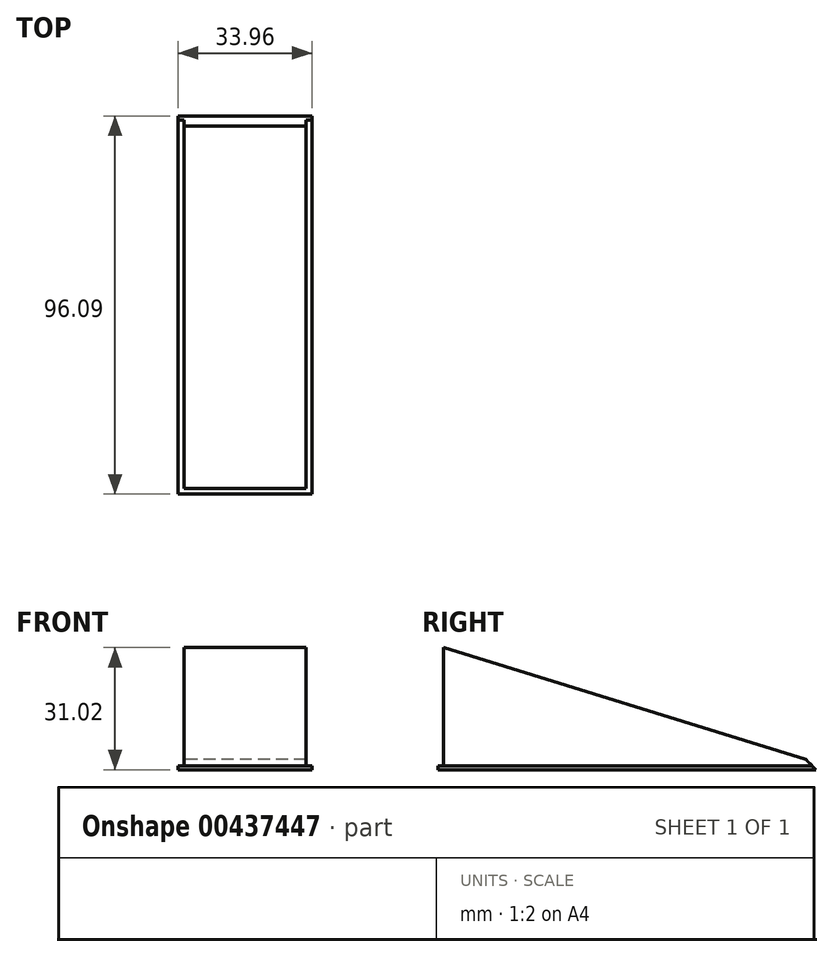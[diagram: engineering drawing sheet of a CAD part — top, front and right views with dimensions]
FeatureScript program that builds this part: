
annotation { "Feature Type Name" : "Feature", "Feature Type Description" : "" }
export const myFeature = defineFeature(function(context is Context, id is Id, definition is map)
    precondition{}
    {
        {
            var Q0;
            Q0=qCreatedBy(makeId("Top.planeOp"),FACE);
            var sketch = newSketch(context, id + "F0", { "sketchPlane" : qUnion([Q0])});
            skLineSegment(sketch, "E0.bottom", {"start": v(16.98, -50.08) * mm, "end": v(-16.98, -50.08) * mm});
            skLineSegment(sketch, "E0.top", {"start": v(16.98, 50.08) * mm, "end": v(-16.98, 50.08) * mm});
            skLineSegment(sketch, "E0.left", {"start": v(16.98, -50.08) * mm, "end": v(16.98, 50.08) * mm});
            skLineSegment(sketch, "E0.right", {"start": v(-16.98, -50.08) * mm, "end": v(-16.98, 50.08) * mm});
            skPoint(sketch, "E0.middle", {"position": v(0, 0) * mm});
            skSolve(sketch);
        }
        {
            var Q0;
            Q0 = qSketchRegion(id + "F0", true);
            extrude(context, id + "F1", {"entities" : qUnion([Q0]), "endBound" : BoundingType.SYMMETRIC, "oppositeDirection" : true, "depth" : 1.02 * mm});
        }
        {
            var Q0;
            Q0=qCreatedBy(makeId("Right.planeOp"),FACE);
            var sketch = newSketch(context, id + "F2", { "sketchPlane" : qUnion([Q0])});
            skLineSegment(sketch, "E1", {"start": v(50.08, 0) * mm, "end": v(-48.64, 30.5) * mm});
            skLineSegment(sketch, "E2", {"start": v(-48.64, 30.5) * mm, "end": v(-48.64, 0) * mm});
            skLineSegment(sketch, "E3", {"start": v(-48.64, 0) * mm, "end": v(50.08, 0) * mm});
            skSolve(sketch);
        }
        {
            var Q0;
            Q0 = qSketchRegion(id + "F2", true);
            extrude(context, id + "F3", {"entities" : qUnion([Q0]), "operationType" : NewBodyOperationType.ADD, "endBound" : BoundingType.SYMMETRIC, "depth" : 30.99 * mm});
        }
        {
            var Q0;
            Q0=makeQuery(id+"F1.opExtrude","CAP_EDGE",EDGE,{"disambiguationData":[OSD([sQuery(id+"F0.wireOp",EDGE,"E0.top")])],"isStart":true});
            chamfer(context, id + "F4", {"entities" : qUnion([Q0]), "width" : 5.08 * mm, "tangentPropagation" : true});
        }
    });
